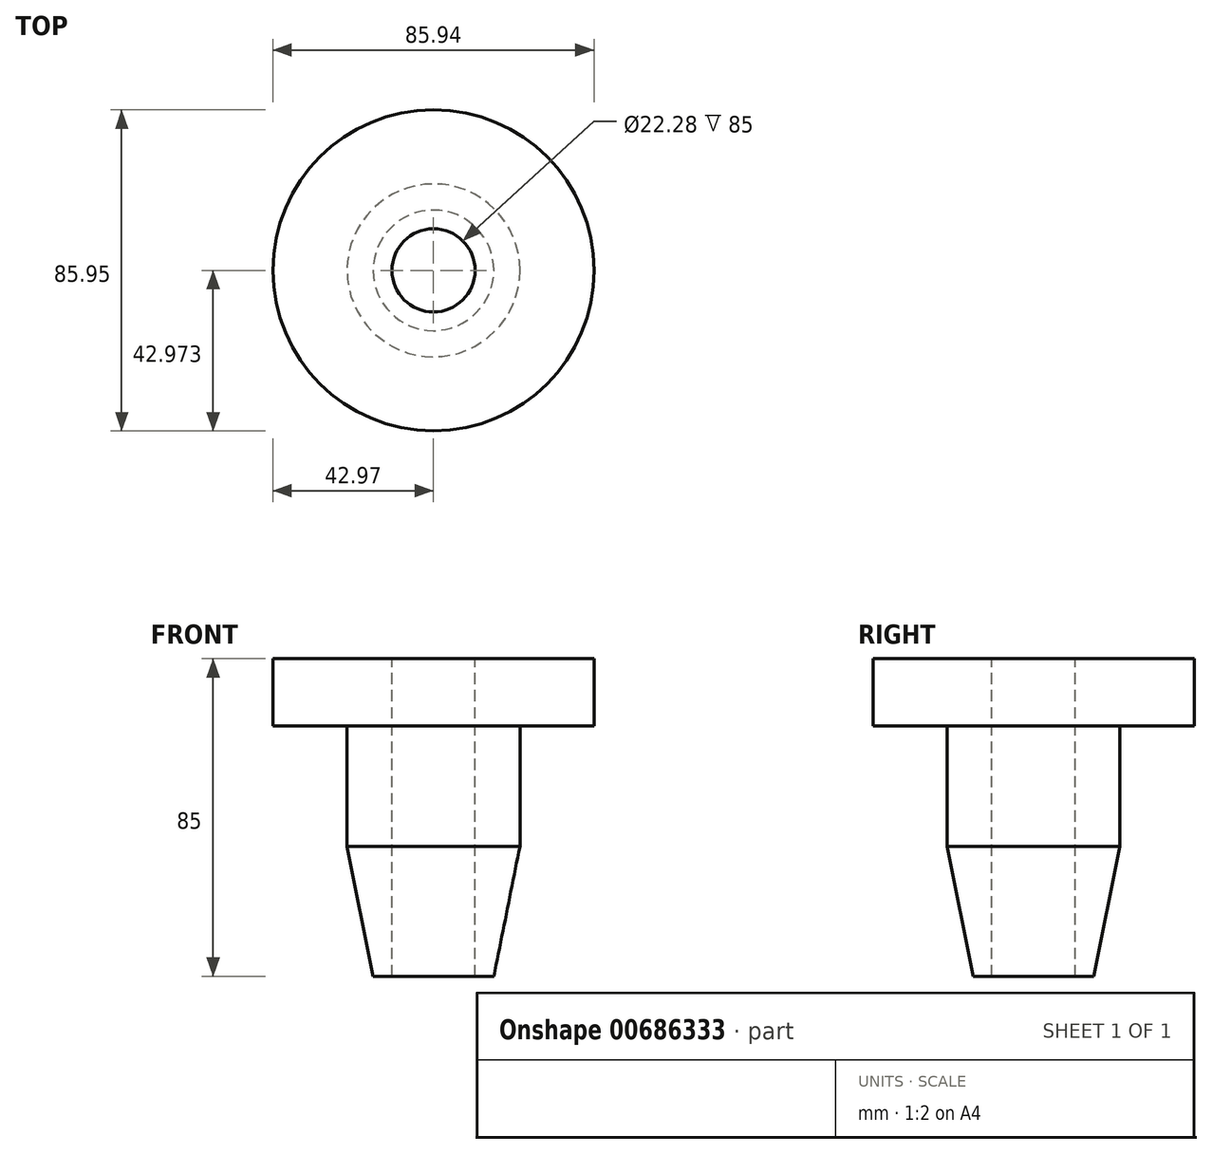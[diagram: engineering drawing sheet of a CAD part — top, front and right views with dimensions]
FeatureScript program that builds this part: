
annotation { "Feature Type Name" : "Feature", "Feature Type Description" : "" }
export const myFeature = defineFeature(function(context is Context, id is Id, definition is map)
    precondition{}
    {
        {
            var Q0;
            Q0=qCreatedBy(makeId("Right.planeOp"),FACE);
            var sketch = newSketch(context, id + "F0", { "sketchPlane" : qUnion([Q0])});
            skLineSegment(sketch, "E0", {"start": v(-5.77, 39.12) * mm, "end": v(26.07, 39.12) * mm});
            skLineSegment(sketch, "E1", {"start": v(26.07, 39.12) * mm, "end": v(26.07, 21.12) * mm});
            skLineSegment(sketch, "E2", {"start": v(26.07, 21.12) * mm, "end": v(6.23, 21.12) * mm});
            skLineSegment(sketch, "E3", {"start": v(6.23, 21.12) * mm, "end": v(6.23, -11.1) * mm});
            skLineSegment(sketch, "E4", {"start": v(-5.77, 39.12) * mm, "end": v(-5.77, -45.88) * mm});
            skLineSegment(sketch, "E5", {"start": v(-0.77, -45.88) * mm, "end": v(6.23, -11.1) * mm});
            skLineSegment(sketch, "E6", {"start": v(-0.77, -45.88) * mm, "end": v(-5.77, -45.88) * mm});
            skLineSegment(sketch, "E7", {"start": v(-16.9, 39.8) * mm, "end": v(-16.9, -46.02) * mm, "construction": true});
            skSolve(sketch);
        }
        {
            var Q0;
            Q0=makeQuery(id+"F0.imprint","IMPRINT",FACE,{"disambiguationData":[TD([[makeQuery(id+"F0.imprint","IMPRINT",EDGE,{"derivedFrom":sQuery(id+"F0.wireOp",EDGE,"E0")}),-1.0]])]});
            var Q1;
            Q1=sQuery(id+"F0.wireOp",EDGE,"E7");
            revolve(context, id + "F1", {"entities" : qUnion([Q0]), "axis" : qUnion([Q1]), "revolveType" : RevolveType.FULL});
        }
    });
